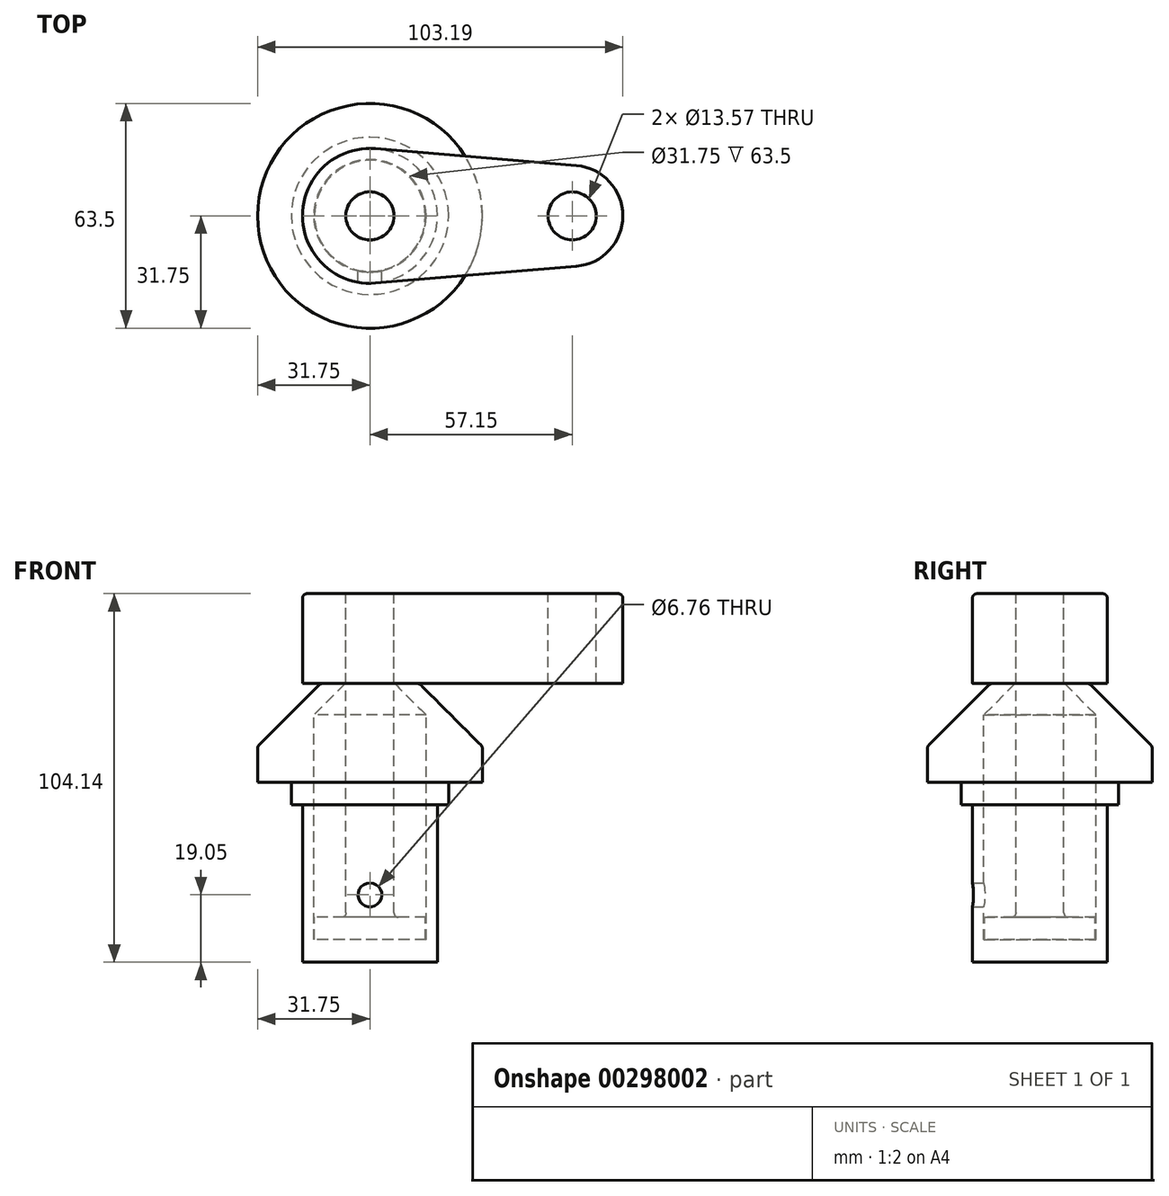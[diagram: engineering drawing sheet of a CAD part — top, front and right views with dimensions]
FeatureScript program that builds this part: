
annotation { "Feature Type Name" : "Feature", "Feature Type Description" : "" }
export const myFeature = defineFeature(function(context is Context, id is Id, definition is map)
    precondition{}
    {
        {
            var Q0;
            Q0=qCreatedBy(makeId("Front.planeOp"),FACE);
            var sketch = newSketch(context, id + "F0", { "sketchPlane" : qUnion([Q0])});
            skLineSegment(sketch, "E0", {"start": v(0, 0) * mm, "end": v(19.05, 0) * mm});
            skLineSegment(sketch, "E1", {"start": v(19.05, 0) * mm, "end": v(19.05, 44.45) * mm});
            skLineSegment(sketch, "E2", {"start": v(19.05, 44.45) * mm, "end": v(22.23, 44.45) * mm});
            skLineSegment(sketch, "E3", {"start": v(22.23, 44.45) * mm, "end": v(22.23, 50.8) * mm});
            skLineSegment(sketch, "E4", {"start": v(22.23, 50.8) * mm, "end": v(31.75, 50.8) * mm});
            skLineSegment(sketch, "E5", {"start": v(31.75, 50.8) * mm, "end": v(31.75, 60.96) * mm});
            skLineSegment(sketch, "E6", {"start": v(31.75, 60.96) * mm, "end": v(13.97, 78.74) * mm});
            skLineSegment(sketch, "E7", {"start": v(13.97, 78.74) * mm, "end": v(0, 78.74) * mm});
            skLineSegment(sketch, "E8", {"start": v(0, 78.74) * mm, "end": v(0, 0) * mm});
            skLineSegment(sketch, "E9", {"start": v(6.98, 78.74) * mm, "end": v(15.87, 69.85) * mm});
            skLineSegment(sketch, "E10", {"start": v(15.87, 69.85) * mm, "end": v(15.88, 6.35) * mm});
            skLineSegment(sketch, "E11", {"start": v(0, 78.74) * mm, "end": v(0, 96.08) * mm, "construction": true});
            skLineSegment(sketch, "E12", {"start": v(6.79, 104.14) * mm, "end": v(6.79, 12.7) * mm});
            skLineSegment(sketch, "E13", {"start": v(6.79, 104.14) * mm, "end": v(0, 104.14) * mm});
            skLineSegment(sketch, "E14", {"start": v(0, 104.14) * mm, "end": v(0, 78.74) * mm});
            skLineSegment(sketch, "E15", {"start": v(0, 6.35) * mm, "end": v(15.88, 6.35) * mm});
            skLineSegment(sketch, "E16", {"start": v(6.79, 12.7) * mm, "end": v(15.68, 12.7) * mm});
            skLineSegment(sketch, "E17", {"start": v(15.68, 12.7) * mm, "end": v(15.68, 6.35) * mm});
            skSolve(sketch);
        }
        {
            var Q0;
            {var subQ0=sQuery(id+"F0.wireOp",EDGE,"E1");Q0=makeQuery(id+"F0.imprint","IMPRINT",FACE,{"disambiguationData":[TD([[makeQuery(id+"F0.imprint","IMPRINT",EDGE,{"derivedFrom":subQ0}),1.0]])]});}
            var Q1;
            {var subQ0=sQuery(id+"F0.wireOp",EDGE,"E8");var subQ1=sQuery(id+"F0.wireOp",EDGE,"E0");var subQ2=makeQuery(id+"F0.imprint","INTERSECT",VERTEX,{"derivedFrom":[subQ1,subQ0]});Q1=makeQuery(id+"F0.imprint","IMPRINT",FACE,{"disambiguationData":[TD([[makeQuery(id+"F0.imprint","IMPRINT",EDGE,{"disambiguationData":[TD([[subQ2,-1.0]])],"derivedFrom":subQ1}),1.0]])]});}
            var Q2;
            Q2=sQuery(id+"F0.wireOp",EDGE,"E8");
            revolve(context, id + "F1", {"entities" : qUnion([Q0, Q1]), "axis" : qUnion([Q2]), "revolveType" : RevolveType.FULL});
        }
        {
            var Q0;
            {var subQ4=sQuery(id+"F0.wireOp",EDGE,"E13");Q0=makeQuery(id+"F0.imprint","IMPRINT",FACE,{"disambiguationData":[TD([[makeQuery(id+"F0.imprint","IMPRINT",EDGE,{"derivedFrom":subQ4}),1.0]])]});}
            var Q1;
            {var subQ0=sQuery(id+"F0.wireOp",EDGE,"E16");Q1=makeQuery(id+"F0.imprint","IMPRINT",FACE,{"disambiguationData":[TD([[makeQuery(id+"F0.imprint","IMPRINT",EDGE,{"derivedFrom":subQ0}),-1.0]])]});}
            var Q2;
            Q2=sQuery(id+"F0.wireOp",EDGE,"E8");
            revolve(context, id + "F2", {"entities" : qUnion([Q0, Q1]), "axis" : qUnion([Q2]), "revolveType" : RevolveType.FULL});
        }
        {
            var Q0;
            Q0=makeQuery(id+"F2.opRevolve","SWEPT_FACE",FACE,{"disambiguationData":[OSD([sQuery(id+"F0.wireOp",EDGE,"E13")])]});
            var sketch = newSketch(context, id + "F3", { "sketchPlane" : qUnion([Q0])});
            skCircle(sketch, "E18.0", {"center": v(0, 0) * mm, "radius": 6.79 * mm});
            skCircle(sketch, "E19", {"center": v(0, 0) * mm, "radius": 19.05 * mm});
            skCircle(sketch, "E20", {"center": v(57.15, 0) * mm, "radius": 14.29 * mm});
            skLineSegment(sketch, "E21", {"start": v(58.34, 14.24) * mm, "end": v(1.59, 18.98) * mm});
            skLineSegment(sketch, "E22", {"start": v(1.59, -18.98) * mm, "end": v(58.34, -14.24) * mm});
            skCircle(sketch, "E23", {"center": v(57.15, 0) * mm, "radius": 6.79 * mm});
            skSolve(sketch);
        }
        {
            var Q0;
            Q0 = qSketchRegion(id + "F3", true);
            var Q1;
            Q1=makeQuery(id+"F1.opRevolve","SWEPT_FACE",FACE,{"disambiguationData":[OSD([sQuery(id+"F0.wireOp",EDGE,"E7")])]});
            extrude(context, id + "F4", {"entities" : qUnion([Q0]), "endBound" : BoundingType.UP_TO_SURFACE, "oppositeDirection" : true, "endBoundEntityFace" : qUnion([Q1]), "depth" : 19.05 * mm});
        }
        {
            var Q0;
            Q0=qCreatedBy(makeId("Front.planeOp"),FACE);
            var sketch = newSketch(context, id + "F5", { "sketchPlane" : qUnion([Q0])});
            skPoint(sketch, "E24", {"position": v(0, 19.05) * mm});
            skSolve(sketch);
        }
        {
            var Q0;
            Q0=sQuery(id+"F5.wireOp",VERTEX,"E24");
            var Q1;
            Q1=makeQuery(id+"F1.opRevolve","SWEPT_BODY",BODY,{"disambiguationData":[OSD([sQuery(id+"F0.wireOp",EDGE,"E0"),sQuery(id+"F0.wireOp",EDGE,"E1"),sQuery(id+"F0.wireOp",EDGE,"E2"),sQuery(id+"F0.wireOp",EDGE,"E3"),sQuery(id+"F0.wireOp",EDGE,"E4"),sQuery(id+"F0.wireOp",EDGE,"E5"),sQuery(id+"F0.wireOp",EDGE,"E6"),sQuery(id+"F0.wireOp",EDGE,"E7"),sQuery(id+"F0.wireOp",EDGE,"E8"),sQuery(id+"F0.wireOp",EDGE,"E9"),sQuery(id+"F0.wireOp",EDGE,"E10"),sQuery(id+"F0.wireOp",EDGE,"E15")])]});
            hole(context, id + "F6", {"style" : HoleStyle.SIMPLE, "endStyle" : HoleEndStyle.THROUGH, "oppositeDirection" : true, "standardTappedOrClearance" : lookupTablePath({ "standard" : "ANSI", "fit" : "Normal (ASME)", "size" : "1/4", "type" : "Clearance" }), "standardBlindInLast" : lookupTablePath({ "fit" : "Free", "standard" : "ANSI", "size" : "1/4", "type" : "Clearance" }), "holeDiameter" : 6.76 * mm, "tappedDepth" : 17.14 * mm, "tapClearance" : 3, "locations" : qUnion([Q0]), "scope" : qUnion([Q1])});
        }
        {
            var Q0;
            Q0=makeQuery(id+"F1.opRevolve","SWEPT_EDGE",EDGE,{"disambiguationData":[OSD([sQuery(id+"F0.wireOp",EDGE,"E6"),sQuery(id+"F0.wireOp",EDGE,"E7")])]});
            var Q1;
            Q1=makeQuery(id+"F1.opRevolve","SWEPT_EDGE",EDGE,{"disambiguationData":[OSD([sQuery(id+"F0.wireOp",EDGE,"E5"),sQuery(id+"F0.wireOp",EDGE,"E6")])]});
            var Q2;
            Q2=makeQuery(id+"F2.opRevolve","SWEPT_EDGE",EDGE,{"disambiguationData":[OSD([sQuery(id+"F0.wireOp",EDGE,"E12"),sQuery(id+"F0.wireOp",EDGE,"E16")])]});
            var Q3;
            Q3=makeQuery(id+"F4.opExtrude","CAP_EDGE",EDGE,{"disambiguationData":[OSD([sQuery(id+"F3.wireOp",EDGE,"E22")])],"isStart":true});
            var Q4;
            {var subQ0=sQuery(id+"F3.wireOp",EDGE,"E20");Q4=makeQuery(id+"F4.opExtrude","TWEAK_EDGE",EDGE,{"derivedFrom":[makeQuery(id+"F1.opRevolve","SWEPT_FACE",FACE,{"disambiguationData":[OSD([sQuery(id+"F0.wireOp",EDGE,"E7")])]}),makeQuery(id+"F3.imprint","IMPRINT",EDGE,{"disambiguationData":[TD([[makeQuery(id+"F3.imprint","INTERSECT",VERTEX,{"derivedFrom":[subQ0,sQuery(id+"F3.wireOp",EDGE,"E21")]}),1.0]])],"derivedFrom":subQ0})]});}
            fillet(context, id + "F7", {"entities" : qUnion([Q0, Q1, Q2, Q3, Q4]), "radius" : 1.27 * mm, "tangentPropagation" : true, "allowEdgeOverflow" : false});
        }
    });
